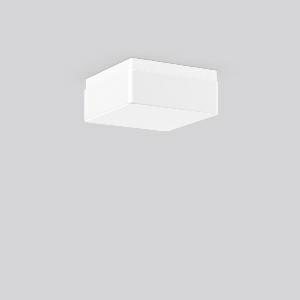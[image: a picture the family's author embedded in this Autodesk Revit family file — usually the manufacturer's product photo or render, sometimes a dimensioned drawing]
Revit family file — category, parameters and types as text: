
# Revit family: quadrat_201412_002_ad8e
name_source: partatom
category: Lighting Fixtures
units: mm (PartAtom-declared; Revit-internal decimal feet)

## family parameters
Cut with Voids When Loaded = No
Host = Face
Light Source = No
Part Type = Normal
Room Calculation Point = No
Round Connector Dimension = Use Diameter
Shared = No

## types (1)
- QUADRAT (1 x LED Modul 830, 990 lm, 3000)
    Apparent Load = 12 VA
    CIE Flux Codes = 38 67 88 80 100
    Color Rendering = 80
    Color Temperature = 3000
    Default Elevation = 1800 mm
    Description = Series: QUADRAT
Square surface-mounted luminaire in classic design. Base: plastic. Opal glass: mouth blown, silk finish. Diffuser fastening: spring system. Suitable for Ceiling mounting, Wall (surface). IP 43 ceiling mounting, IP 44 wall mounting. 
Colour: white
Length: 280 mm
Width: 280 mm
Height: 120 mm
Lamp: LED exchangeable
Socket: without socket
Colour temperature: 3000K
Colour rendering index (CRI): 83
System power: 12 W
Rated luminous flux: 990 lm
Luminous efficiency: 83 lm/W
Control gear: AC Strom, dim.Ph.an-/abschnitt
Protection class: I
Type of protection: IP 43
    Height = 120 mm
    Lamp = 1 x LED Modul 830
    Lamp Light Flux = 990 lm
    Lamp count = 1
    Length = 280 mm
    Lifetime = 50000 h
    Luminous efficacy = 83 lm/W
    Manufacturer = RZB
    ModVariant = No
    Model = 201412.002
    Mounting Place = Ceiling, Wall
    Mounting Type = Surface mounted
    Number of Poles = 1
    OnlyDefault = Yes
    Power Factor = 1
    Product Name = QUADRAT
    Product group = Surface mounted ceiling and wall luminaires
    ProductGroupID = 305
    Protection Class = Protection class I
    Protection Degree = IP 43
    RLX_Detail_Level = 1
    RLX_Emergency_Light_Flux = 0 lm
    RLX_Emergency_Type = 0
    RLX_Emergency_Type_DB = No
    RlxData = <blob elided: 11465 chars, md5=bdcd1336>
    Socket = socket
    Standby Power = 0 W
    System Light Flux = 990 lm
    System Power = 12 W
    Type Comments = Product without accessories
    Type Image = 20129.002.jpg
    URL = http://relux.com
    VarID = ---
    Voltage = 230 V
    Voltage Range = 220-240 V
    Weight = 0.00 kg
    Width = 280 mm

## geometry (parser evidence)
native form markers: Sweep x12
no freeform markers — native parametric forms only
